# Revit family: NLRS_23_GM_WPB_HS27R gevelbekleding_jazo_jazo
name_source: partatom
category: Generic Models
units: mm (PartAtom-declared; Revit-internal decimal feet)

## family parameters
Always vertical = No
Can host rebar = No
Cut with Voids When Loaded = No
OmniClass Number = 23.30.60.11.17.11
OmniClass Title = Fixed Exterior Louvers and Grilles
Part Type = Normal
Room Calculation Point = No
Round Connector Dimension = Use Diameter
Shared = No
Work Plane-Based = Yes

## types (1)
- TYPECATALOG
    Assembly Code = 23.30.60.11.17.11
    Default Elevation = 0 mm  [stored 0 ft]
    Description = HS27R gevelbekleding
    JAZO_C_materiaal bevestiging gevelbekleding = <By Category>
    JAZO_C_materiaal schoep = <By Category>
    JAZO_C_opbouwrooster HS27R = Yes
    Manufacturer = JAZO Zevenaar bv
    Model = HS27R gevelbekleding
    NLRS_C_content_datum gewijzigd = 9-11-2022
    NLRS_C_content_datum uitgifte = 17-8-2022
    NLRS_C_content_provider = JAZO Zevenaar bv
    NLRS_C_content_revit versie = REVIT 2020.2
    NLRS_C_content_versie = 2.3
    NLRS_C_diepte_02 = 25 mm  [stored 0.082021 ft]
    NLRS_C_diepte_max = 325 mm  [stored 1.06627 ft]
    NLRS_C_diepte_min = 41 mm  [stored 0.134514 ft]
    NLRS_C_hoogte_min = 360 mm  [stored 1.1811 ft]
    NLRS_C_leverancier_adres = Handelsdwarsstraat 10
    NLRS_C_leverancier_bedrijfsnaam = JAZO Zevenaar bv
    NLRS_C_leverancier_plaats = Zevenaar
    NLRS_C_leverancier_postcode = 6905 DJ
    NLRS_C_leverancier_telefoonnummer = +31 316 - 59 29 11
    NLRS_C_leverancier_url = www.jazo.com
    NLRS_C_stelruimte = 5 mm  [stored 0.0164042 ft]
    URL = www.jazo.com

note: [stored X ft] marks values corroborated as IEEE doubles in the binary element streams (Revit-internal decimal feet)

## geometry (parser evidence)
native form markers: Sweep x31
no freeform markers — native parametric forms only
